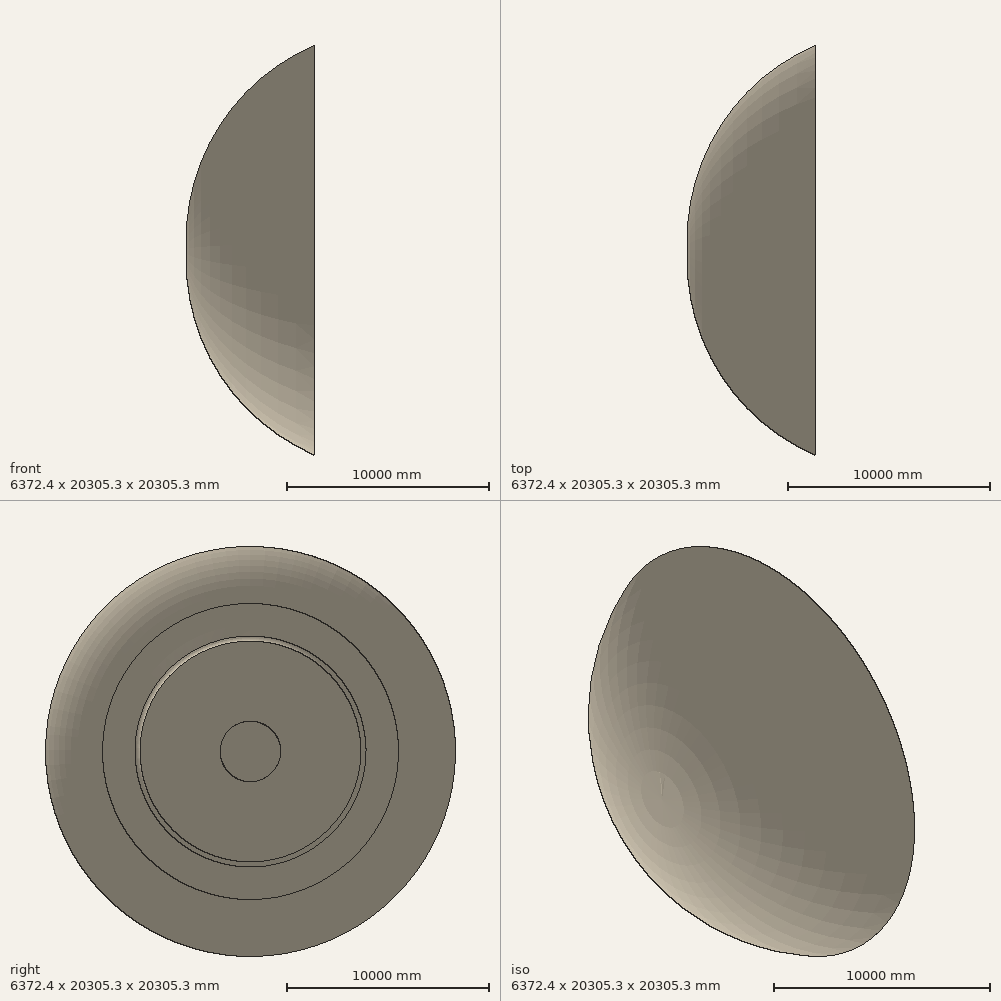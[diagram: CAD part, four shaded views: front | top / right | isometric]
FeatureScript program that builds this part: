
annotation { "Feature Type Name" : "Feature", "Feature Type Description" : "" }
export const myFeature = defineFeature(function(context is Context, id is Id, definition is map)
    precondition{}
    {
        {
            var Q0;
            Q0=qCreatedBy(makeId("Front.planeOp"),FACE);
            var sketch = newSketch(context, id + "F0", { "sketchPlane" : qUnion([Q0])});
            skArc(sketch, "E0", {"start": v(9447.36, -5497.45) * mm, "mid": v(4944.22, 3626.26) * mm, "end": v(-5178.36, 4652.76) * mm});
            skArc(sketch, "E1", {"start": v(-5178.36, 4652.76) * mm, "mid": v(-6589.16, 3489.9) * mm, "end": v(-7357.78, 1831.05) * mm});
            skArc(sketch, "E2", {"start": v(-7357.78, 1831.05) * mm, "mid": v(-7411.48, 1003.66) * mm, "end": v(-7685.77, 221.22) * mm});
            skArc(sketch, "E3", {"start": v(-7685.77, 221.22) * mm, "mid": v(-8127.28, -32.17) * mm, "end": v(-8538.04, 268.5) * mm});
            skArc(sketch, "E4", {"start": v(-8538.04, 268.5) * mm, "mid": v(-8694.81, 358.66) * mm, "end": v(-8814.03, 222.66) * mm});
            skLineSegment(sketch, "E5", {"start": v(-8814.03, 222.67) * mm, "end": v(-8814.03, -4000.63) * mm});
            skLineSegment(sketch, "E6", {"start": v(-8814.03, -4000.63) * mm, "end": v(-9459.03, -4000.63) * mm});
            skLineSegment(sketch, "E7", {"start": v(-9459.03, -4000.63) * mm, "end": v(-9459.03, -5500.63) * mm});
            skLineSegment(sketch, "E8", {"start": v(9447.36, -5497.45) * mm, "end": v(-9459.03, -5500.63) * mm});
            skLineSegment(sketch, "E9", {"start": v(9447.36, -5497.45) * mm, "end": v(-1044.13, -5499.22) * mm});
            skSolve(sketch);
        }
        {
            var Q0;
            Q0=sQuery(id+"F0.wireOp",EDGE,"E5");
            var Q1;
            Q1=sQuery(id+"F0.wireOp",EDGE,"E3");
            var Q2;
            Q2=sQuery(id+"F0.wireOp",EDGE,"E2");
            var Q3;
            Q3=sQuery(id+"F0.wireOp",EDGE,"E1");
            var Q4;
            Q4=sQuery(id+"F0.wireOp",EDGE,"E0");
            var Q5;
            Q5=sQuery(id+"F0.wireOp",EDGE,"E7");
            var Q6;
            Q6=sQuery(id+"F0.wireOp",EDGE,"E6");
            var Q7;
            Q7=sQuery(id+"F0.wireOp",EDGE,"E4");
            var Q8;
            Q8=sQuery(id+"F0.wireOp",EDGE,"E8");
            revolve(context, id + "F1", {"bodyType" : ToolBodyType.SURFACE, "surfaceEntities" : qUnion([Q0, Q1, Q2, Q3, Q4, Q5, Q6, Q7]), "axis" : qUnion([Q8]), "revolveType" : RevolveType.FULL});
        }
    });
